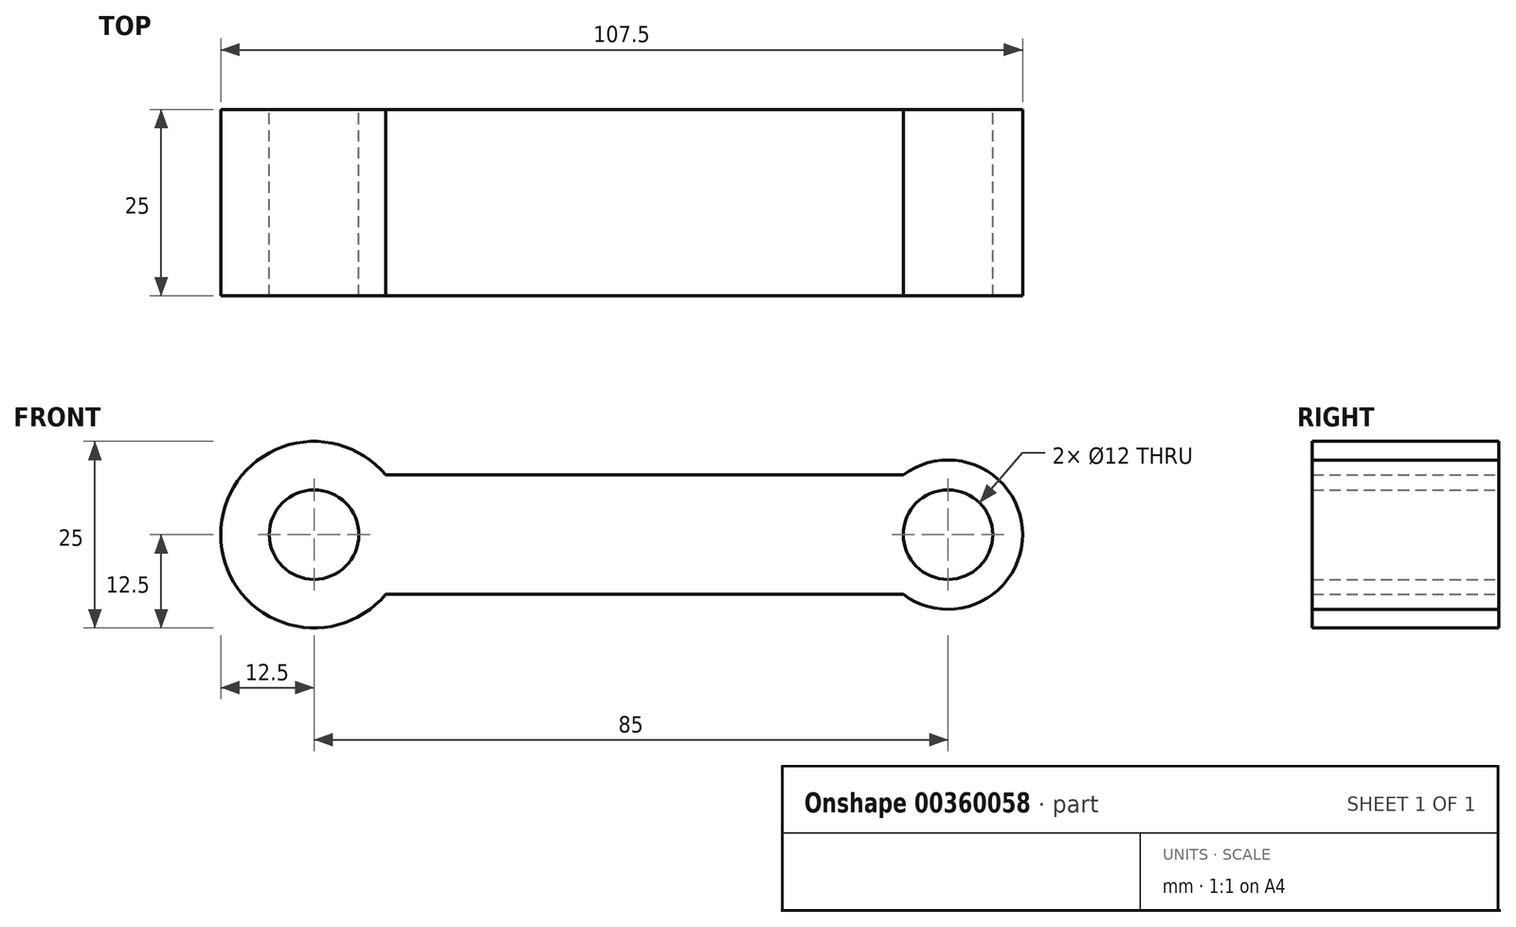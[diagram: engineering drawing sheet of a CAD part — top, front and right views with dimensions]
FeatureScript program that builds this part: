
annotation { "Feature Type Name" : "Feature", "Feature Type Description" : "" }
export const myFeature = defineFeature(function(context is Context, id is Id, definition is map)
    precondition{}
    {
        {
            var Q0;
            Q0=qCreatedBy(makeId("Front.planeOp"),FACE);
            var sketch = newSketch(context, id + "F0", { "sketchPlane" : qUnion([Q0])});
            skCircle(sketch, "E0", {"center": v(0, 0) * mm, "radius": 12.5 * mm});
            skCircle(sketch, "E1", {"center": v(85, 0) * mm, "radius": 10 * mm});
            skLineSegment(sketch, "E2", {"start": v(0, 0) * mm, "end": v(85, 0) * mm});
            skLineSegment(sketch, "E3", {"start": v(9.6, 8) * mm, "end": v(79, 8) * mm});
            skLineSegment(sketch, "E4.MirrorCS", {"start": v(9.6, -8) * mm, "end": v(79, -8) * mm});
            skCircle(sketch, "E5", {"center": v(0, 0) * mm, "radius": 6 * mm});
            skCircle(sketch, "E6", {"center": v(85, 0) * mm, "radius": 6 * mm});
            skSolve(sketch);
        }
        {
            var Q0;
            Q0 = qSketchRegion(id + "F0", true);
            extrude(context, id + "F1", {"entities" : qUnion([Q0]), "depth" : 25 * mm});
        }
    });
